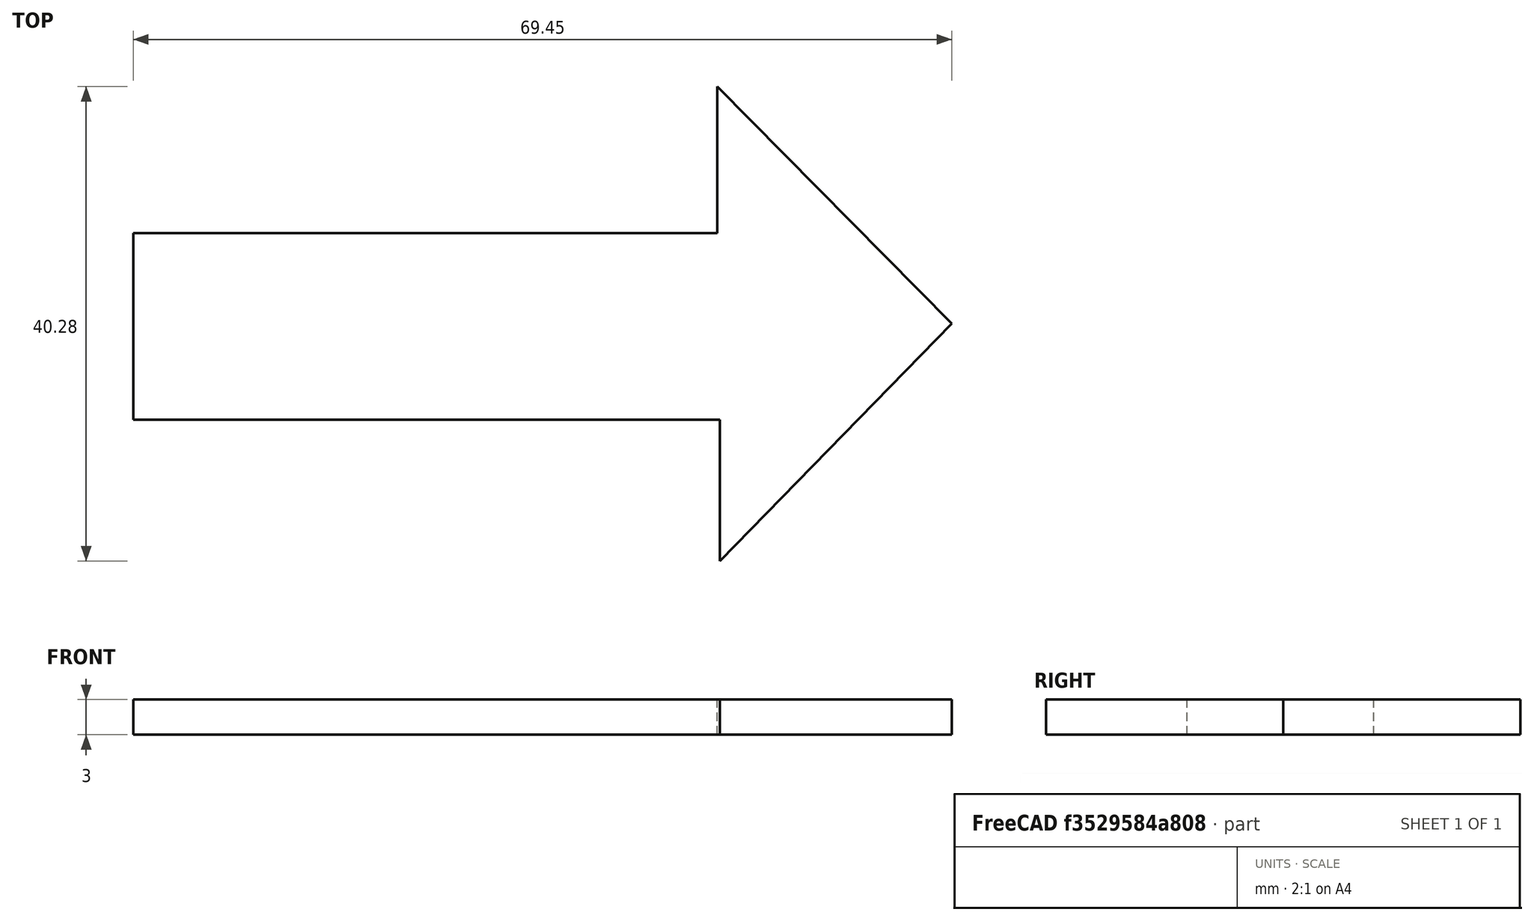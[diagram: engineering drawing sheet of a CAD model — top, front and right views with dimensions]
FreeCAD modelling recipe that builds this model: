
FCSTD DOCUMENT  (FreeCAD 0.21R33694 (Git))
Label: OJT1_T016R02_ fletxa
License: All rights reserved
LicenseURL: http://en.wikipedia.org/wiki/All_rights_reserved
objects: Sketcher::SketchObject×1, PartDesign::Pad×1, PartDesign::Body×1
note: 4 computed .brp shape members not serialized (recipe doc carries the construction recipe); baked Part::Feature solids carry a one-line shape summary decoded from their .brp

FEATURE [Sketcher::SketchObject] Sketch
  FullyConstrained = false
  MapMode = 5
  Support = -> [XY_Plane]
  sketch-geometry (7):
    g0: LineSegment StartX=29.8643 StartY=0 StartZ=0 EndX=9.95475 EndY=20.1357 EndZ=0
    g1: LineSegment StartX=9.95475 StartY=20.1357 StartZ=0 EndX=9.95475 EndY=7.69231 EndZ=0
    g2: LineSegment StartX=9.95475 StartY=7.69231 StartZ=0 EndX=-39.5928 EndY=7.69231 EndZ=0
    g3: LineSegment StartX=-39.5928 StartY=7.69231 StartZ=0 EndX=-39.5928 EndY=-8.1448 EndZ=0
    g4: LineSegment StartX=-39.5928 StartY=-8.1448 StartZ=0 EndX=10.181 EndY=-8.1448 EndZ=0
    g5: LineSegment StartX=10.181 StartY=-8.1448 StartZ=0 EndX=10.181 EndY=-20.1357 EndZ=0
    g6: LineSegment StartX=10.181 StartY=-20.1357 StartZ=0 EndX=29.8643 EndY=0 EndZ=0
  constraints (13):
    c: PointOnObject(g0,g-1)
    c: Coincident(g0,g1)
    c: Vertical(g1)
    c: Coincident(g1,g2)
    c: Horizontal(g2)
    c: Coincident(g2,g3)
    c: Vertical(g3)
    c: Coincident(g3,g4)
    c: Horizontal(g4)
    c: Coincident(g4,g5)
    c: Vertical(g5)
    c: Coincident(g5,g6)
    c: PointOnObject(g6,g-1)
FEATURE [PartDesign::Pad] Pad
  Direction = (0,0,1)
  Length = 3
  Length2 = 10
  Profile = -> Sketch
  ReferenceAxis = -> Sketch [N_Axis]
  Type = 0
FEATURE [PartDesign::Body] Body
  Group = -> [Sketch,Pad]
  Origin = -> Origin
  Tip = -> Pad
